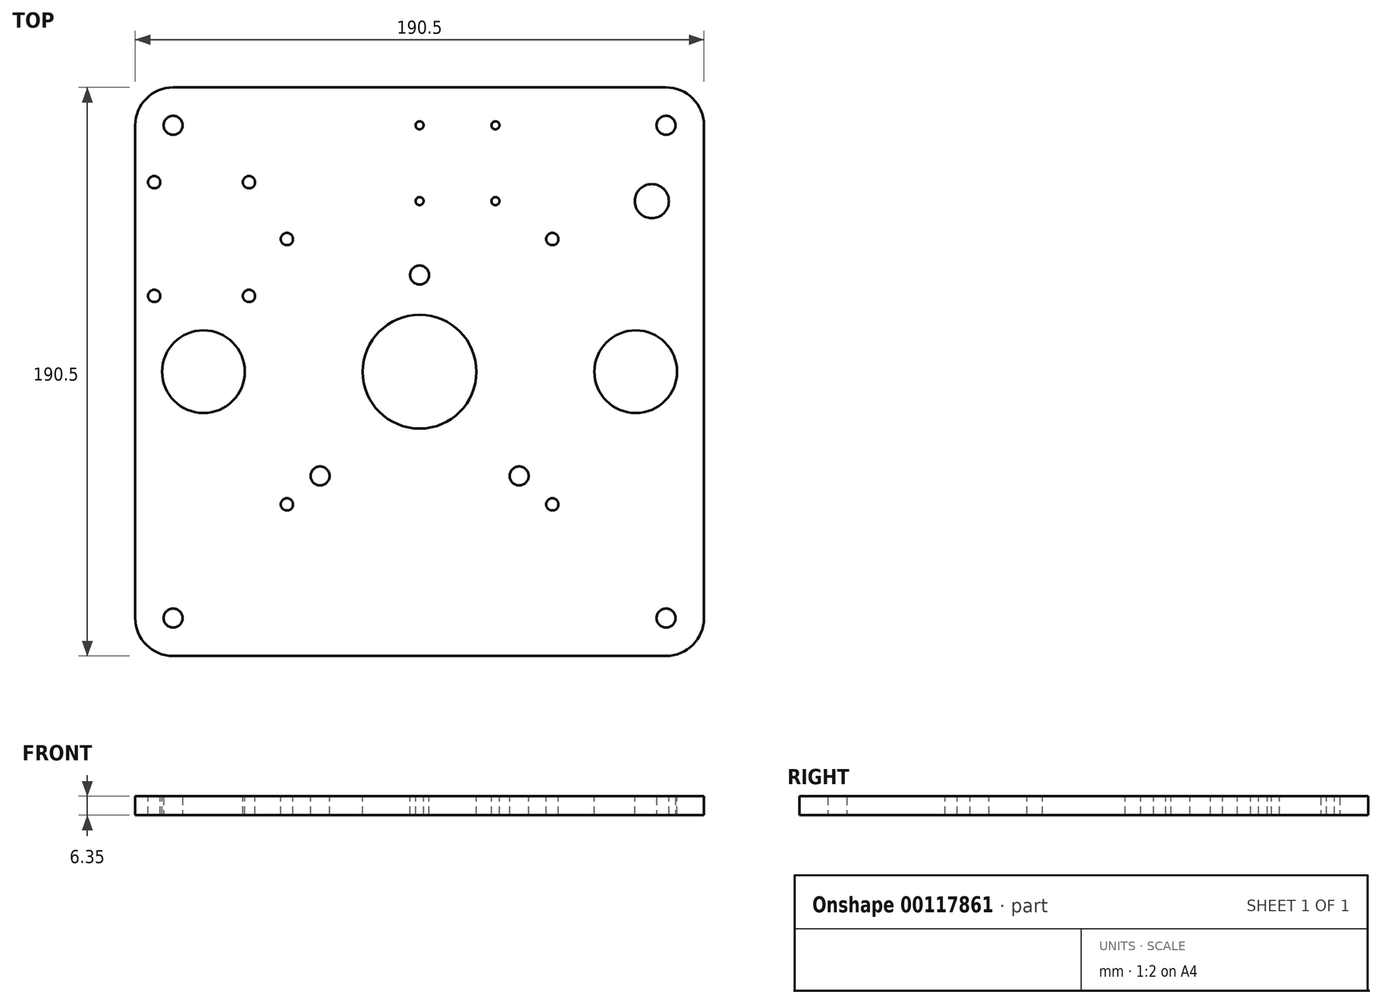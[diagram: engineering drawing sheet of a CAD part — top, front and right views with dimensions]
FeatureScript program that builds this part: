
annotation { "Feature Type Name" : "Feature", "Feature Type Description" : "" }
export const myFeature = defineFeature(function(context is Context, id is Id, definition is map)
    precondition{}
    {
        {
            var Q0;
            Q0=qCreatedBy(makeId("Top.planeOp"),FACE);
            var sketch = newSketch(context, id + "F0", { "sketchPlane" : qUnion([Q0])});
            skLineSegment(sketch, "E0.bottom", {"start": v(95.25, 95.25) * mm, "end": v(-95.25, 95.25) * mm});
            skLineSegment(sketch, "E0.top", {"start": v(95.25, -95.25) * mm, "end": v(-95.25, -95.25) * mm});
            skLineSegment(sketch, "E0.left", {"start": v(95.25, 95.25) * mm, "end": v(95.25, -95.25) * mm});
            skLineSegment(sketch, "E0.right", {"start": v(-95.25, 95.25) * mm, "end": v(-95.25, -95.25) * mm});
            skPoint(sketch, "E0.middle", {"position": v(0, 0) * mm});
            skLineSegment(sketch, "E1", {"start": v(0, 95.25) * mm, "end": v(0, -95.25) * mm, "construction": true});
            skLineSegment(sketch, "E2", {"start": v(-95.25, 0) * mm, "end": v(95.25, 0) * mm, "construction": true});
            skCircle(sketch, "E3", {"center": v(-82.55, 82.55) * mm, "radius": 3.18 * mm});
            skCircle(sketch, "E4.MirrorC", {"center": v(82.55, 82.55) * mm, "radius": 3.18 * mm});
            skCircle(sketch, "E5.MirrorC", {"center": v(-82.55, -82.55) * mm, "radius": 3.18 * mm});
            skCircle(sketch, "E6.MirrorC", {"center": v(82.55, -82.55) * mm, "radius": 3.18 * mm});
            skSolve(sketch);
        }
        {
            var Q0;
            Q0 = qSketchRegion(id + "F0", true);
            extrude(context, id + "F1", {"entities" : qUnion([Q0]), "depth" : 6.35 * mm});
        }
        {
            var Q0;
            Q0=makeQuery(id+"F1.opExtrude","CAP_FACE",FACE,{"disambiguationData":[OSD([sQuery(id+"F0.wireOp",EDGE,"E0.bottom"),sQuery(id+"F0.wireOp",EDGE,"E0.top"),sQuery(id+"F0.wireOp",EDGE,"E0.left"),sQuery(id+"F0.wireOp",EDGE,"E0.right"),sQuery(id+"F0.wireOp",EDGE,"E3"),sQuery(id+"F0.wireOp",EDGE,"E4.MirrorC"),sQuery(id+"F0.wireOp",EDGE,"E5.MirrorC"),sQuery(id+"F0.wireOp",EDGE,"E6.MirrorC")])],"isStart":false});
            var sketch = newSketch(context, id + "F2", { "sketchPlane" : qUnion([Q0])});
            skLineSegment(sketch, "E7.bottom", {"start": v(-88.9, 63.5) * mm, "end": v(-57.15, 63.5) * mm});
            skLineSegment(sketch, "E7.top", {"start": v(-88.9, 25.4) * mm, "end": v(-57.15, 25.4) * mm});
            skLineSegment(sketch, "E7.left", {"start": v(-88.9, 63.5) * mm, "end": v(-88.9, 25.4) * mm});
            skLineSegment(sketch, "E7.right", {"start": v(-57.15, 63.5) * mm, "end": v(-57.15, 25.4) * mm});
            skCircle(sketch, "E8", {"center": v(-88.9, 63.5) * mm, "radius": 2.06 * mm});
            skCircle(sketch, "E9", {"center": v(-57.15, 63.5) * mm, "radius": 2.06 * mm});
            skCircle(sketch, "E10", {"center": v(-57.15, 25.4) * mm, "radius": 2.06 * mm});
            skCircle(sketch, "E11", {"center": v(-88.9, 25.4) * mm, "radius": 2.06 * mm});
            skSolve(sketch);
        }
        {
            var Q0;
            {var subQ0=sQuery(id+"F2.wireOp",EDGE,"E7.left");var subQ1=sQuery(id+"F2.wireOp",EDGE,"E7.bottom");var subQ2=makeQuery(id+"F2.imprint","INTERSECT",VERTEX,{"derivedFrom":[subQ1,subQ0]});Q0=makeQuery(id+"F2.imprint","IMPRINT",FACE,{"disambiguationData":[TD([[makeQuery(id+"F2.imprint","IMPRINT",EDGE,{"disambiguationData":[TD([[subQ2,-1.0]])],"derivedFrom":subQ1}),1.0]])]});}
            var Q1;
            {var subQ0=sQuery(id+"F2.wireOp",EDGE,"E7.left");var subQ1=sQuery(id+"F2.wireOp",EDGE,"E7.bottom");var subQ2=makeQuery(id+"F2.imprint","INTERSECT",VERTEX,{"derivedFrom":[subQ1,subQ0]});Q1=makeQuery(id+"F2.imprint","IMPRINT",FACE,{"disambiguationData":[TD([[makeQuery(id+"F2.imprint","IMPRINT",EDGE,{"disambiguationData":[TD([[subQ2,-1.0]])],"derivedFrom":subQ1}),-1.0]])]});}
            var Q2;
            {var subQ0=sQuery(id+"F2.wireOp",EDGE,"E7.right");var subQ1=sQuery(id+"F2.wireOp",EDGE,"E7.bottom");var subQ2=makeQuery(id+"F2.imprint","INTERSECT",VERTEX,{"derivedFrom":[subQ1,subQ0]});Q2=makeQuery(id+"F2.imprint","IMPRINT",FACE,{"disambiguationData":[TD([[makeQuery(id+"F2.imprint","IMPRINT",EDGE,{"disambiguationData":[TD([[subQ2,1.0]])],"derivedFrom":subQ1}),-1.0]])]});}
            var Q3;
            {var subQ0=sQuery(id+"F2.wireOp",EDGE,"E7.right");var subQ1=sQuery(id+"F2.wireOp",EDGE,"E7.bottom");var subQ2=makeQuery(id+"F2.imprint","INTERSECT",VERTEX,{"derivedFrom":[subQ1,subQ0]});Q3=makeQuery(id+"F2.imprint","IMPRINT",FACE,{"disambiguationData":[TD([[makeQuery(id+"F2.imprint","IMPRINT",EDGE,{"disambiguationData":[TD([[subQ2,1.0]])],"derivedFrom":subQ1}),1.0]])]});}
            var Q4;
            {var subQ0=sQuery(id+"F2.wireOp",EDGE,"E7.left");var subQ1=sQuery(id+"F2.wireOp",EDGE,"E7.top");var subQ2=makeQuery(id+"F2.imprint","INTERSECT",VERTEX,{"derivedFrom":[subQ1,subQ0]});Q4=makeQuery(id+"F2.imprint","IMPRINT",FACE,{"disambiguationData":[TD([[makeQuery(id+"F2.imprint","IMPRINT",EDGE,{"disambiguationData":[TD([[subQ2,-1.0]])],"derivedFrom":subQ1}),1.0]])]});}
            var Q5;
            {var subQ0=sQuery(id+"F2.wireOp",EDGE,"E7.left");var subQ1=sQuery(id+"F2.wireOp",EDGE,"E7.top");var subQ2=makeQuery(id+"F2.imprint","INTERSECT",VERTEX,{"derivedFrom":[subQ1,subQ0]});Q5=makeQuery(id+"F2.imprint","IMPRINT",FACE,{"disambiguationData":[TD([[makeQuery(id+"F2.imprint","IMPRINT",EDGE,{"disambiguationData":[TD([[subQ2,-1.0]])],"derivedFrom":subQ1}),-1.0]])]});}
            var Q6;
            {var subQ0=sQuery(id+"F2.wireOp",EDGE,"E7.right");var subQ1=sQuery(id+"F2.wireOp",EDGE,"E7.top");var subQ2=makeQuery(id+"F2.imprint","INTERSECT",VERTEX,{"derivedFrom":[subQ1,subQ0]});Q6=makeQuery(id+"F2.imprint","IMPRINT",FACE,{"disambiguationData":[TD([[makeQuery(id+"F2.imprint","IMPRINT",EDGE,{"disambiguationData":[TD([[subQ2,1.0]])],"derivedFrom":subQ1}),1.0]])]});}
            var Q7;
            {var subQ0=sQuery(id+"F2.wireOp",EDGE,"E7.right");var subQ1=sQuery(id+"F2.wireOp",EDGE,"E7.top");var subQ2=makeQuery(id+"F2.imprint","INTERSECT",VERTEX,{"derivedFrom":[subQ1,subQ0]});Q7=makeQuery(id+"F2.imprint","IMPRINT",FACE,{"disambiguationData":[TD([[makeQuery(id+"F2.imprint","IMPRINT",EDGE,{"disambiguationData":[TD([[subQ2,1.0]])],"derivedFrom":subQ1}),-1.0]])]});}
            extrude(context, id + "F3", {"entities" : qUnion([Q0, Q1, Q2, Q3, Q4, Q5, Q6, Q7]), "operationType" : NewBodyOperationType.REMOVE, "endBound" : BoundingType.THROUGH_ALL, "oppositeDirection" : true, "depth" : 25.4 * mm});
        }
        {
            var Q0;
            Q0=makeQuery(id+"F1.opExtrude","CAP_FACE",FACE,{"disambiguationData":[OSD([sQuery(id+"F0.wireOp",EDGE,"E0.bottom"),sQuery(id+"F0.wireOp",EDGE,"E0.top"),sQuery(id+"F0.wireOp",EDGE,"E0.left"),sQuery(id+"F0.wireOp",EDGE,"E0.right"),sQuery(id+"F0.wireOp",EDGE,"E3"),sQuery(id+"F0.wireOp",EDGE,"E4.MirrorC"),sQuery(id+"F0.wireOp",EDGE,"E5.MirrorC"),sQuery(id+"F0.wireOp",EDGE,"E6.MirrorC")])],"isStart":false});
            var sketch = newSketch(context, id + "F4", { "sketchPlane" : qUnion([Q0])});
            skLineSegment(sketch, "E12.bottom", {"start": v(-44.45, -44.45) * mm, "end": v(44.45, -44.45) * mm});
            skLineSegment(sketch, "E12.top", {"start": v(-44.45, 44.45) * mm, "end": v(44.45, 44.45) * mm});
            skLineSegment(sketch, "E12.left", {"start": v(-44.45, -44.45) * mm, "end": v(-44.45, 44.45) * mm});
            skLineSegment(sketch, "E12.right", {"start": v(44.45, -44.45) * mm, "end": v(44.45, 44.45) * mm});
            skCircle(sketch, "E13", {"center": v(-44.45, 44.45) * mm, "radius": 2.06 * mm});
            skCircle(sketch, "E14", {"center": v(44.45, 44.45) * mm, "radius": 2.06 * mm});
            skCircle(sketch, "E15", {"center": v(44.45, -44.45) * mm, "radius": 2.06 * mm});
            skCircle(sketch, "E16", {"center": v(-44.45, -44.45) * mm, "radius": 2.06 * mm});
            skLineSegment(sketch, "E17", {"start": v(0, 44.45) * mm, "end": v(0, -44.45) * mm, "construction": true});
            skLineSegment(sketch, "E18", {"start": v(-44.45, 0) * mm, "end": v(44.45, 0) * mm, "construction": true});
            skSolve(sketch);
        }
        {
            var Q0;
            {var subQ0=sQuery(id+"F4.wireOp",EDGE,"E12.left");var subQ1=sQuery(id+"F4.wireOp",EDGE,"E12.bottom");var subQ2=makeQuery(id+"F4.imprint","INTERSECT",VERTEX,{"derivedFrom":[subQ1,subQ0]});Q0=makeQuery(id+"F4.imprint","IMPRINT",FACE,{"disambiguationData":[TD([[makeQuery(id+"F4.imprint","IMPRINT",EDGE,{"disambiguationData":[TD([[subQ2,-1.0]])],"derivedFrom":subQ1}),1.0]])]});}
            var Q1;
            {var subQ0=sQuery(id+"F4.wireOp",EDGE,"E12.left");var subQ1=sQuery(id+"F4.wireOp",EDGE,"E12.bottom");var subQ2=makeQuery(id+"F4.imprint","INTERSECT",VERTEX,{"derivedFrom":[subQ1,subQ0]});Q1=makeQuery(id+"F4.imprint","IMPRINT",FACE,{"disambiguationData":[TD([[makeQuery(id+"F4.imprint","IMPRINT",EDGE,{"disambiguationData":[TD([[subQ2,-1.0]])],"derivedFrom":subQ1}),-1.0]])]});}
            var Q2;
            {var subQ0=sQuery(id+"F4.wireOp",EDGE,"E12.right");var subQ1=sQuery(id+"F4.wireOp",EDGE,"E12.bottom");var subQ2=makeQuery(id+"F4.imprint","INTERSECT",VERTEX,{"derivedFrom":[subQ1,subQ0]});Q2=makeQuery(id+"F4.imprint","IMPRINT",FACE,{"disambiguationData":[TD([[makeQuery(id+"F4.imprint","IMPRINT",EDGE,{"disambiguationData":[TD([[subQ2,1.0]])],"derivedFrom":subQ1}),1.0]])]});}
            var Q3;
            {var subQ0=sQuery(id+"F4.wireOp",EDGE,"E12.right");var subQ1=sQuery(id+"F4.wireOp",EDGE,"E12.bottom");var subQ2=makeQuery(id+"F4.imprint","INTERSECT",VERTEX,{"derivedFrom":[subQ1,subQ0]});Q3=makeQuery(id+"F4.imprint","IMPRINT",FACE,{"disambiguationData":[TD([[makeQuery(id+"F4.imprint","IMPRINT",EDGE,{"disambiguationData":[TD([[subQ2,1.0]])],"derivedFrom":subQ1}),-1.0]])]});}
            var Q4;
            {var subQ0=sQuery(id+"F4.wireOp",EDGE,"E12.left");var subQ1=sQuery(id+"F4.wireOp",EDGE,"E12.top");var subQ2=makeQuery(id+"F4.imprint","INTERSECT",VERTEX,{"derivedFrom":[subQ1,subQ0]});Q4=makeQuery(id+"F4.imprint","IMPRINT",FACE,{"disambiguationData":[TD([[makeQuery(id+"F4.imprint","IMPRINT",EDGE,{"disambiguationData":[TD([[subQ2,-1.0]])],"derivedFrom":subQ1}),1.0]])]});}
            var Q5;
            {var subQ0=sQuery(id+"F4.wireOp",EDGE,"E12.left");var subQ1=sQuery(id+"F4.wireOp",EDGE,"E12.top");var subQ2=makeQuery(id+"F4.imprint","INTERSECT",VERTEX,{"derivedFrom":[subQ1,subQ0]});Q5=makeQuery(id+"F4.imprint","IMPRINT",FACE,{"disambiguationData":[TD([[makeQuery(id+"F4.imprint","IMPRINT",EDGE,{"disambiguationData":[TD([[subQ2,-1.0]])],"derivedFrom":subQ1}),-1.0]])]});}
            var Q6;
            {var subQ0=sQuery(id+"F4.wireOp",EDGE,"E12.right");var subQ1=sQuery(id+"F4.wireOp",EDGE,"E12.top");var subQ2=makeQuery(id+"F4.imprint","INTERSECT",VERTEX,{"derivedFrom":[subQ1,subQ0]});Q6=makeQuery(id+"F4.imprint","IMPRINT",FACE,{"disambiguationData":[TD([[makeQuery(id+"F4.imprint","IMPRINT",EDGE,{"disambiguationData":[TD([[subQ2,1.0]])],"derivedFrom":subQ1}),-1.0]])]});}
            var Q7;
            {var subQ0=sQuery(id+"F4.wireOp",EDGE,"E12.right");var subQ1=sQuery(id+"F4.wireOp",EDGE,"E12.top");var subQ2=makeQuery(id+"F4.imprint","INTERSECT",VERTEX,{"derivedFrom":[subQ1,subQ0]});Q7=makeQuery(id+"F4.imprint","IMPRINT",FACE,{"disambiguationData":[TD([[makeQuery(id+"F4.imprint","IMPRINT",EDGE,{"disambiguationData":[TD([[subQ2,1.0]])],"derivedFrom":subQ1}),1.0]])]});}
            extrude(context, id + "F5", {"entities" : qUnion([Q0, Q1, Q2, Q3, Q4, Q5, Q6, Q7]), "operationType" : NewBodyOperationType.REMOVE, "endBound" : BoundingType.THROUGH_ALL, "oppositeDirection" : true, "depth" : 25.4 * mm});
        }
        {
            var Q0;
            Q0=makeQuery(id+"F1.opExtrude","CAP_FACE",FACE,{"disambiguationData":[OSD([sQuery(id+"F0.wireOp",EDGE,"E0.bottom"),sQuery(id+"F0.wireOp",EDGE,"E0.top"),sQuery(id+"F0.wireOp",EDGE,"E0.left"),sQuery(id+"F0.wireOp",EDGE,"E0.right"),sQuery(id+"F0.wireOp",EDGE,"E3"),sQuery(id+"F0.wireOp",EDGE,"E4.MirrorC"),sQuery(id+"F0.wireOp",EDGE,"E5.MirrorC"),sQuery(id+"F0.wireOp",EDGE,"E6.MirrorC")])],"isStart":false});
            var sketch = newSketch(context, id + "F6", { "sketchPlane" : qUnion([Q0])});
            skCircle(sketch, "E19", {"center": v(77.79, 57.15) * mm, "radius": 5.72 * mm});
            skSolve(sketch);
        }
        {
            var Q0;
            Q0 = qSketchRegion(id + "F6", true);
            extrude(context, id + "F7", {"entities" : qUnion([Q0]), "operationType" : NewBodyOperationType.REMOVE, "endBound" : BoundingType.THROUGH_ALL, "oppositeDirection" : true, "depth" : 25.4 * mm});
        }
        {
            var Q0;
            Q0=makeQuery(id+"F1.opExtrude","CAP_FACE",FACE,{"disambiguationData":[OSD([sQuery(id+"F0.wireOp",EDGE,"E0.bottom"),sQuery(id+"F0.wireOp",EDGE,"E0.top"),sQuery(id+"F0.wireOp",EDGE,"E0.left"),sQuery(id+"F0.wireOp",EDGE,"E0.right"),sQuery(id+"F0.wireOp",EDGE,"E3"),sQuery(id+"F0.wireOp",EDGE,"E4.MirrorC"),sQuery(id+"F0.wireOp",EDGE,"E5.MirrorC"),sQuery(id+"F0.wireOp",EDGE,"E6.MirrorC")])],"isStart":false});
            var sketch = newSketch(context, id + "F8", { "sketchPlane" : qUnion([Q0])});
            skLineSegment(sketch, "E20", {"start": v(-44.45, 44.45) * mm, "end": v(-44.45, -44.45) * mm, "construction": true});
            skLineSegment(sketch, "E21", {"start": v(-44.45, -44.45) * mm, "end": v(44.45, -44.45) * mm, "construction": true});
            skLineSegment(sketch, "E22", {"start": v(44.45, -44.45) * mm, "end": v(44.45, 44.45) * mm, "construction": true});
            skLineSegment(sketch, "E23", {"start": v(44.45, 44.45) * mm, "end": v(-44.45, 44.45) * mm, "construction": true});
            skLineSegment(sketch, "E24", {"start": v(-44.45, -34.92) * mm, "end": v(44.45, -34.92) * mm, "construction": true});
            skLineSegment(sketch, "E25", {"start": v(-44.45, 32.39) * mm, "end": v(44.45, 32.39) * mm, "construction": true});
            skLineSegment(sketch, "E26", {"start": v(0, 44.45) * mm, "end": v(0, -44.45) * mm, "construction": true});
            skCircle(sketch, "E27", {"center": v(0, 0) * mm, "radius": 19.05 * mm});
            skCircle(sketch, "E28", {"center": v(-33.34, -34.92) * mm, "radius": 3.18 * mm});
            skCircle(sketch, "E29", {"center": v(33.34, -34.92) * mm, "radius": 3.18 * mm});
            skCircle(sketch, "E30", {"center": v(0, 32.39) * mm, "radius": 3.18 * mm});
            skSolve(sketch);
        }
        {
            var Q0;
            Q0=makeQuery(id+"F8.imprint","IMPRINT",FACE,{"disambiguationData":[TD([[makeQuery(id+"F8.imprint","IMPRINT",EDGE,{"derivedFrom":sQuery(id+"F8.wireOp",EDGE,"E28")}),1.0]])]});
            var Q1;
            Q1=makeQuery(id+"F8.imprint","IMPRINT",FACE,{"disambiguationData":[TD([[makeQuery(id+"F8.imprint","IMPRINT",EDGE,{"derivedFrom":sQuery(id+"F8.wireOp",EDGE,"E29")}),1.0]])]});
            var Q2;
            Q2=makeQuery(id+"F8.imprint","IMPRINT",FACE,{"disambiguationData":[TD([[makeQuery(id+"F8.imprint","IMPRINT",EDGE,{"derivedFrom":sQuery(id+"F8.wireOp",EDGE,"E30")}),1.0]])]});
            var Q3;
            Q3=makeQuery(id+"F8.imprint","IMPRINT",FACE,{"disambiguationData":[TD([[makeQuery(id+"F8.imprint","IMPRINT",EDGE,{"derivedFrom":sQuery(id+"F8.wireOp",EDGE,"E27")}),1.0]])]});
            extrude(context, id + "F9", {"entities" : qUnion([Q0, Q1, Q2, Q3]), "operationType" : NewBodyOperationType.REMOVE, "endBound" : BoundingType.THROUGH_ALL, "oppositeDirection" : true, "depth" : 25.4 * mm});
        }
        {
            var Q0;
            Q0=makeQuery(id+"F1.opExtrude","SWEPT_EDGE",EDGE,{"disambiguationData":[OSD([sQuery(id+"F0.wireOp",EDGE,"E0.bottom"),sQuery(id+"F0.wireOp",EDGE,"E0.right")])]});
            var Q1;
            Q1=makeQuery(id+"F1.opExtrude","SWEPT_EDGE",EDGE,{"disambiguationData":[OSD([sQuery(id+"F0.wireOp",EDGE,"E0.bottom"),sQuery(id+"F0.wireOp",EDGE,"E0.left")])]});
            var Q2;
            Q2=makeQuery(id+"F1.opExtrude","SWEPT_EDGE",EDGE,{"disambiguationData":[OSD([sQuery(id+"F0.wireOp",EDGE,"E0.top"),sQuery(id+"F0.wireOp",EDGE,"E0.left")])]});
            var Q3;
            Q3=makeQuery(id+"F1.opExtrude","SWEPT_EDGE",EDGE,{"disambiguationData":[OSD([sQuery(id+"F0.wireOp",EDGE,"E0.top"),sQuery(id+"F0.wireOp",EDGE,"E0.right")])]});
            fillet(context, id + "F10", {"entities" : qUnion([Q0, Q1, Q2, Q3]), "radius" : 12.7 * mm, "tangentPropagation" : true, "allowEdgeOverflow" : false});
        }
        {
            var Q0;
            Q0=makeQuery(id+"F1.opExtrude","CAP_FACE",FACE,{"disambiguationData":[OSD([sQuery(id+"F0.wireOp",EDGE,"E0.bottom"),sQuery(id+"F0.wireOp",EDGE,"E0.top"),sQuery(id+"F0.wireOp",EDGE,"E0.left"),sQuery(id+"F0.wireOp",EDGE,"E0.right"),sQuery(id+"F0.wireOp",EDGE,"E3"),sQuery(id+"F0.wireOp",EDGE,"E4.MirrorC"),sQuery(id+"F0.wireOp",EDGE,"E5.MirrorC"),sQuery(id+"F0.wireOp",EDGE,"E6.MirrorC")])],"isStart":false});
            var sketch = newSketch(context, id + "F11", { "sketchPlane" : qUnion([Q0])});
            skLineSegment(sketch, "E31.bottom", {"start": v(0, 82.55) * mm, "end": v(25.4, 82.55) * mm});
            skLineSegment(sketch, "E31.top", {"start": v(0, 57.15) * mm, "end": v(25.4, 57.15) * mm});
            skLineSegment(sketch, "E31.left", {"start": v(0, 82.55) * mm, "end": v(0, 57.15) * mm});
            skLineSegment(sketch, "E31.right", {"start": v(25.4, 82.55) * mm, "end": v(25.4, 57.15) * mm});
            skLineSegment(sketch, "E32.bottom", {"start": v(-6.35, 88.9) * mm, "end": v(31.75, 88.9) * mm});
            skLineSegment(sketch, "E32.top", {"start": v(-6.35, 50.8) * mm, "end": v(31.75, 50.8) * mm});
            skLineSegment(sketch, "E32.left", {"start": v(-6.35, 88.9) * mm, "end": v(-6.35, 50.8) * mm});
            skLineSegment(sketch, "E32.right", {"start": v(31.75, 88.9) * mm, "end": v(31.75, 50.8) * mm});
            skCircle(sketch, "E33", {"center": v(0, 82.55) * mm, "radius": 1.35 * mm});
            skCircle(sketch, "E34", {"center": v(25.4, 82.55) * mm, "radius": 1.35 * mm});
            skCircle(sketch, "E35", {"center": v(25.4, 57.15) * mm, "radius": 1.35 * mm});
            skCircle(sketch, "E36", {"center": v(0, 57.15) * mm, "radius": 1.35 * mm});
            skSolve(sketch);
        }
        {
            var Q0;
            {var subQ0=sQuery(id+"F11.wireOp",EDGE,"E31.left");var subQ1=sQuery(id+"F11.wireOp",EDGE,"E31.bottom");var subQ2=makeQuery(id+"F11.imprint","INTERSECT",VERTEX,{"derivedFrom":[subQ1,subQ0]});Q0=makeQuery(id+"F11.imprint","IMPRINT",FACE,{"disambiguationData":[TD([[makeQuery(id+"F11.imprint","IMPRINT",EDGE,{"disambiguationData":[TD([[subQ2,-1.0]])],"derivedFrom":subQ1}),1.0]])]});}
            var Q1;
            {var subQ0=sQuery(id+"F11.wireOp",EDGE,"E31.right");var subQ1=sQuery(id+"F11.wireOp",EDGE,"E31.bottom");var subQ2=makeQuery(id+"F11.imprint","INTERSECT",VERTEX,{"derivedFrom":[subQ1,subQ0]});Q1=makeQuery(id+"F11.imprint","IMPRINT",FACE,{"disambiguationData":[TD([[makeQuery(id+"F11.imprint","IMPRINT",EDGE,{"disambiguationData":[TD([[subQ2,1.0]])],"derivedFrom":subQ1}),1.0]])]});}
            var Q2;
            {var subQ0=sQuery(id+"F11.wireOp",EDGE,"E31.right");var subQ1=sQuery(id+"F11.wireOp",EDGE,"E31.top");var subQ2=makeQuery(id+"F11.imprint","INTERSECT",VERTEX,{"derivedFrom":[subQ1,subQ0]});Q2=makeQuery(id+"F11.imprint","IMPRINT",FACE,{"disambiguationData":[TD([[makeQuery(id+"F11.imprint","IMPRINT",EDGE,{"disambiguationData":[TD([[subQ2,1.0]])],"derivedFrom":subQ1}),-1.0]])]});}
            var Q3;
            {var subQ0=sQuery(id+"F11.wireOp",EDGE,"E31.right");var subQ1=sQuery(id+"F11.wireOp",EDGE,"E31.bottom");var subQ2=makeQuery(id+"F11.imprint","INTERSECT",VERTEX,{"derivedFrom":[subQ1,subQ0]});Q3=makeQuery(id+"F11.imprint","IMPRINT",FACE,{"disambiguationData":[TD([[makeQuery(id+"F11.imprint","IMPRINT",EDGE,{"disambiguationData":[TD([[subQ2,1.0]])],"derivedFrom":subQ1}),-1.0]])]});}
            var Q4;
            {var subQ0=sQuery(id+"F11.wireOp",EDGE,"E31.right");var subQ1=sQuery(id+"F11.wireOp",EDGE,"E31.top");var subQ2=makeQuery(id+"F11.imprint","INTERSECT",VERTEX,{"derivedFrom":[subQ1,subQ0]});Q4=makeQuery(id+"F11.imprint","IMPRINT",FACE,{"disambiguationData":[TD([[makeQuery(id+"F11.imprint","IMPRINT",EDGE,{"disambiguationData":[TD([[subQ2,1.0]])],"derivedFrom":subQ1}),1.0]])]});}
            var Q5;
            {var subQ0=sQuery(id+"F11.wireOp",EDGE,"E31.left");var subQ1=sQuery(id+"F11.wireOp",EDGE,"E31.top");var subQ2=makeQuery(id+"F11.imprint","INTERSECT",VERTEX,{"derivedFrom":[subQ1,subQ0]});Q5=makeQuery(id+"F11.imprint","IMPRINT",FACE,{"disambiguationData":[TD([[makeQuery(id+"F11.imprint","IMPRINT",EDGE,{"disambiguationData":[TD([[subQ2,-1.0]])],"derivedFrom":subQ1}),1.0]])]});}
            var Q6;
            {var subQ0=sQuery(id+"F11.wireOp",EDGE,"E31.left");var subQ1=sQuery(id+"F11.wireOp",EDGE,"E31.top");var subQ2=makeQuery(id+"F11.imprint","INTERSECT",VERTEX,{"derivedFrom":[subQ1,subQ0]});Q6=makeQuery(id+"F11.imprint","IMPRINT",FACE,{"disambiguationData":[TD([[makeQuery(id+"F11.imprint","IMPRINT",EDGE,{"disambiguationData":[TD([[subQ2,-1.0]])],"derivedFrom":subQ1}),-1.0]])]});}
            var Q7;
            {var subQ0=sQuery(id+"F11.wireOp",EDGE,"E31.left");var subQ1=sQuery(id+"F11.wireOp",EDGE,"E31.bottom");var subQ2=makeQuery(id+"F11.imprint","INTERSECT",VERTEX,{"derivedFrom":[subQ1,subQ0]});Q7=makeQuery(id+"F11.imprint","IMPRINT",FACE,{"disambiguationData":[TD([[makeQuery(id+"F11.imprint","IMPRINT",EDGE,{"disambiguationData":[TD([[subQ2,-1.0]])],"derivedFrom":subQ1}),-1.0]])]});}
            extrude(context, id + "F12", {"entities" : qUnion([Q0, Q1, Q2, Q3, Q4, Q5, Q6, Q7]), "operationType" : NewBodyOperationType.REMOVE, "endBound" : BoundingType.THROUGH_ALL, "oppositeDirection" : true, "depth" : 25.4 * mm});
        }
        {
            var Q0;
            Q0=makeQuery(id+"F2.imprint","IMPRINT",FACE,{"disambiguationData":[TD([[makeQuery(id+"F2.imprint","IMPRINT",EDGE,{"derivedFrom":makeQuery(id+"F1.opExtrude","CAP_EDGE",EDGE,{"disambiguationData":[OSD([sQuery(id+"F0.wireOp",EDGE,"E0.bottom")])],"isStart":false})}),1.0]])]});
            var sketch = newSketch(context, id + "F13", { "sketchPlane" : qUnion([Q0])});
            skCircle(sketch, "E37", {"center": v(-72.4, 0) * mm, "radius": 13.84 * mm});
            skCircle(sketch, "E38", {"center": v(72.4, 0) * mm, "radius": 13.84 * mm});
            skSolve(sketch);
        }
        {
            var Q0;
            Q0 = qSketchRegion(id + "F13", true);
            extrude(context, id + "F14", {"entities" : qUnion([Q0]), "operationType" : NewBodyOperationType.REMOVE, "endBound" : BoundingType.THROUGH_ALL, "oppositeDirection" : true, "depth" : 25.4 * mm});
        }
    });
